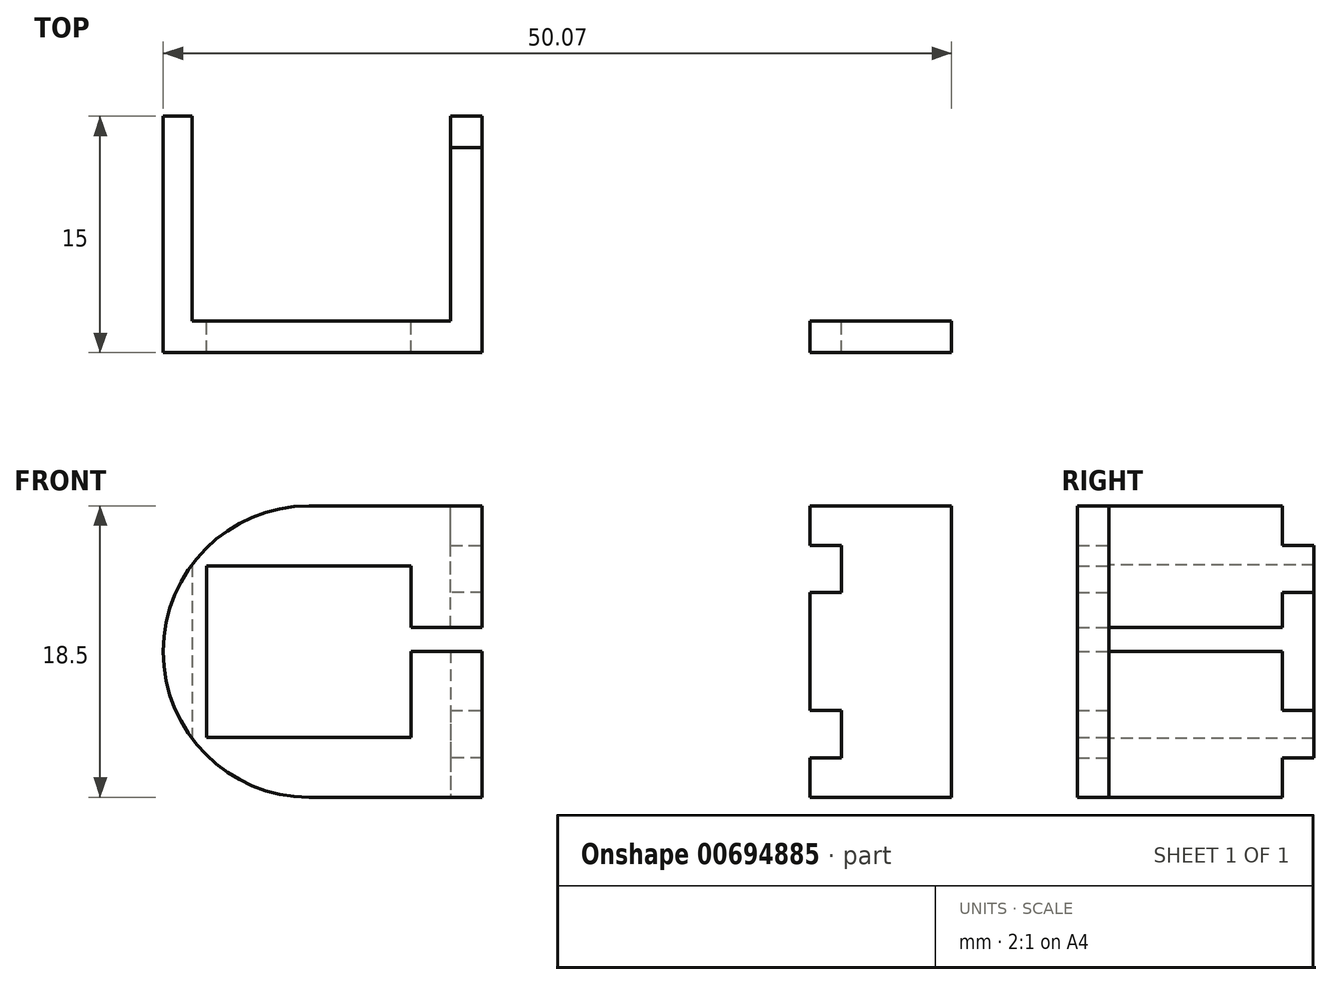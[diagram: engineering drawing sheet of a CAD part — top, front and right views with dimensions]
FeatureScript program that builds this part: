
annotation { "Feature Type Name" : "Feature", "Feature Type Description" : "" }
export const myFeature = defineFeature(function(context is Context, id is Id, definition is map)
    precondition{}
    {
        {
            var Q0;
            Q0=qCreatedBy(makeId("Front.planeOp"),FACE);
            var sketch = newSketch(context, id + "F0", { "sketchPlane" : qUnion([Q0])});
            skArc(sketch, "E0.MirrorCS", {"start": v(27.93, 0) * mm, "mid": v(18.68, 9.25) * mm, "end": v(27.93, 18.5) * mm});
            skLineSegment(sketch, "E1.MirrorCS", {"start": v(20.5, 14.75) * mm, "end": v(20.5, 3.75) * mm});
            skLineSegment(sketch, "E2.MirrorCS", {"start": v(21.43, 14.7) * mm, "end": v(21.43, 3.8) * mm});
            skLineSegment(sketch, "E3.MirrorCS", {"start": v(34.43, 14.7) * mm, "end": v(21.43, 14.7) * mm});
            skLineSegment(sketch, "E4.MirrorCS", {"start": v(34.43, 3.8) * mm, "end": v(21.43, 3.8) * mm});
            skLineSegment(sketch, "E5.MirrorCS", {"start": v(34.43, 9.27) * mm, "end": v(34.43, 3.8) * mm});
            skLineSegment(sketch, "E6.MirrorCS", {"start": v(34.43, 10.77) * mm, "end": v(34.43, 14.7) * mm});
            skLineSegment(sketch, "E7.MirrorCS", {"start": v(34.43, 10.77) * mm, "end": v(38.93, 10.77) * mm});
            skLineSegment(sketch, "E8.MirrorCS", {"start": v(38.93, 9.27) * mm, "end": v(34.43, 9.27) * mm});
            skLineSegment(sketch, "E9.MirrorCS", {"start": v(36.93, 9.27) * mm, "end": v(36.93, 0) * mm});
            skLineSegment(sketch, "E10.MirrorCS", {"start": v(38.93, 18.5) * mm, "end": v(38.93, 0) * mm});
            skLineSegment(sketch, "E11.MirrorCS", {"start": v(38.93, 13) * mm, "end": v(36.93, 13) * mm});
            skLineSegment(sketch, "E12.MirrorCS", {"start": v(36.93, 16) * mm, "end": v(38.93, 16) * mm});
            skLineSegment(sketch, "E13.MirrorCS", {"start": v(38.93, 18.5) * mm, "end": v(36.93, 18.5) * mm});
            skLineSegment(sketch, "E14.MirrorCS", {"start": v(27.93, 18.5) * mm, "end": v(38.93, 18.5) * mm});
            skLineSegment(sketch, "E15.MirrorCS", {"start": v(27.93, 0) * mm, "end": v(38.93, 0) * mm});
            skLineSegment(sketch, "E16.MirrorCS", {"start": v(36.93, 10.77) * mm, "end": v(36.93, 18.5) * mm});
            skLineSegment(sketch, "E17.MirrorCS", {"start": v(36.93, 5.5) * mm, "end": v(38.93, 5.5) * mm});
            skLineSegment(sketch, "E18.MirrorCS", {"start": v(38.93, 2.5) * mm, "end": v(36.93, 2.5) * mm});
            skLineSegment(sketch, "E19.MirrorCS", {"start": v(59.75, 18.5) * mm, "end": v(61.75, 18.5) * mm});
            skLineSegment(sketch, "E20.MirrorCS", {"start": v(59.75, 18.5) * mm, "end": v(59.75, 16) * mm});
            skLineSegment(sketch, "E21.MirrorCS", {"start": v(61.75, 16) * mm, "end": v(59.75, 16) * mm});
            skLineSegment(sketch, "E22.MirrorCS", {"start": v(59.75, 16) * mm, "end": v(59.75, 18.5) * mm});
            skLineSegment(sketch, "E23.MirrorCS", {"start": v(61.75, 13) * mm, "end": v(61.75, 16) * mm});
            skLineSegment(sketch, "E24.MirrorCS", {"start": v(59.75, 13) * mm, "end": v(61.75, 13) * mm});
            skLineSegment(sketch, "E25.MirrorCS", {"start": v(59.75, 16) * mm, "end": v(59.75, 13.5) * mm});
            skLineSegment(sketch, "E26.MirrorCS", {"start": v(61.75, 5.5) * mm, "end": v(59.75, 5.5) * mm});
            skLineSegment(sketch, "E27.MirrorCS", {"start": v(61.75, 2.5) * mm, "end": v(59.75, 2.5) * mm});
            skLineSegment(sketch, "E28.MirrorCS", {"start": v(59.75, 0) * mm, "end": v(59.75, 18.5) * mm});
            skLineSegment(sketch, "E29.MirrorCS", {"start": v(68.75, 0) * mm, "end": v(68.75, 18.5) * mm});
            skLineSegment(sketch, "E30.MirrorCS", {"start": v(59.75, 0) * mm, "end": v(68.75, 0) * mm});
            skLineSegment(sketch, "E31.MirrorCS", {"start": v(61.75, 0) * mm, "end": v(61.75, 18.5) * mm});
            skLineSegment(sketch, "E32.MirrorCS", {"start": v(59.75, 18.5) * mm, "end": v(68.75, 18.5) * mm});
            skLineSegment(sketch, "E33.MirrorCS", {"start": v(38.93, 10.77) * mm, "end": v(38.93, 9.27) * mm});
            skLineSegment(sketch, "E34.MirrorCS", {"start": v(36.93, 18.5) * mm, "end": v(36.93, 16) * mm});
            skLineSegment(sketch, "E35.MirrorCS", {"start": v(36.93, 13) * mm, "end": v(36.93, 16) * mm});
            skPoint(sketch, "E36.MirrorP", {"position": v(37.93, 13) * mm});
            skLineSegment(sketch, "E37.MirrorCS", {"start": v(27.93, 0) * mm, "end": v(27.93, 18.5) * mm});
            skSolve(sketch);
        }
        {
            var Q0;
            {var subQ3=sQuery(id+"F0.wireOp",EDGE,"kESMrQ5b-ams2-7Oer-iUNR-JSe8RSim2Rgg");Q0=makeQuery(id+"F0.imprint","IMPRINT",FACE,{"disambiguationData":[TD([[makeQuery(id+"F0.imprint","IMPRINT",EDGE,{"derivedFrom":subQ3}),-1.0]])]});}
            var Q1;
            {var subQ12=sQuery(id+"F0.wireOp",EDGE,"Yr70NcdM-JPDj-xeuz-Pe8b-xZYOvRdpObg3.top");Q1=makeQuery(id+"F0.imprint","IMPRINT",FACE,{"disambiguationData":[TD([[makeQuery(id+"F0.imprint","IMPRINT",EDGE,{"derivedFrom":subQ12}),1.0]])]});}
            var Q2;
            {var subQ0=sQuery(id+"F0.wireOp",EDGE,"UIRKKA4R-8CtD-udC1-kdKj-49Blse4cZEUQ");Q2=makeQuery(id+"F0.imprint","IMPRINT",FACE,{"disambiguationData":[TD([[makeQuery(id+"F0.imprint","IMPRINT",EDGE,{"derivedFrom":subQ0}),-1.0]])]});}
            var Q3;
            {var subQ0=sQuery(id+"F0.wireOp",EDGE,"kkTMgRkU-buEo-ValQ-K1kS-Wfla19uNzp3g");Q3=makeQuery(id+"F0.imprint","IMPRINT",FACE,{"disambiguationData":[TD([[makeQuery(id+"F0.imprint","IMPRINT",EDGE,{"derivedFrom":subQ0}),-1.0]])]});}
            var Q4;
            {var subQ5=sQuery(id+"F0.wireOp",EDGE,"umQxmC7r-UdGl-FK5S-hts2-lfyIpxZBKDAi");Q4=makeQuery(id+"F0.imprint","IMPRINT",FACE,{"disambiguationData":[TD([[makeQuery(id+"F0.imprint","IMPRINT",EDGE,{"derivedFrom":subQ5}),-1.0]])]});}
            var Q5;
            {var subQ0=sQuery(id+"F0.wireOp",EDGE,"kNnYodP8-lzwz-CTh5-yjqH-wt2QJZLzKjdq");Q5=makeQuery(id+"F0.imprint","IMPRINT",FACE,{"disambiguationData":[TD([[makeQuery(id+"F0.imprint","IMPRINT",EDGE,{"derivedFrom":subQ0}),1.0]])]});}
            var Q6;
            {var subQ0=sQuery(id+"F0.wireOp",EDGE,"b358ca5a-2aeb-42fa-86b1-f23f205046210.MirrorCS");Q6=makeQuery(id+"F0.imprint","IMPRINT",FACE,{"disambiguationData":[TD([[makeQuery(id+"F0.imprint","IMPRINT",EDGE,{"derivedFrom":subQ0}),1.0]])]});}
            var Q7;
            {var subQ0=sQuery(id+"F0.wireOp",EDGE,"kESMrQ5b-ams2-7Oer-iUNR-JSe8RSim2Rgg");Q7=makeQuery(id+"F0.imprint","IMPRINT",FACE,{"disambiguationData":[TD([[makeQuery(id+"F0.imprint","IMPRINT",EDGE,{"derivedFrom":subQ0}),1.0]])]});}
            var Q8;
            {var subQ0=sQuery(id+"F0.wireOp",EDGE,"Gw2HPYI3-RblX-RLRO-vnwY-24Af2lyYfVmX");Q8=makeQuery(id+"F0.imprint","IMPRINT",FACE,{"disambiguationData":[TD([[makeQuery(id+"F0.imprint","IMPRINT",EDGE,{"derivedFrom":subQ0}),1.0]])]});}
            var Q9;
            {var subQ5=sQuery(id+"F0.wireOp",EDGE,"HoU1y5w9-Mg6P-dM28-ahBt-uTMt5Gy9G0wr.top");Q9=makeQuery(id+"F0.imprint","IMPRINT",FACE,{"disambiguationData":[TD([[makeQuery(id+"F0.imprint","IMPRINT",EDGE,{"derivedFrom":subQ5}),1.0]])]});}
            var Q10;
            {var subQ0=sQuery(id+"F0.wireOp",EDGE,"Eh2vApwt-d02c-R8fF-7La6-7nooEkv2mVzI");Q10=makeQuery(id+"F0.imprint","IMPRINT",FACE,{"disambiguationData":[TD([[makeQuery(id+"F0.imprint","IMPRINT",EDGE,{"derivedFrom":subQ0}),-1.0]])]});}
            var Q11;
            {var subQ5=sQuery(id+"F0.wireOp",EDGE,"BYSS7cPW-qHzp-sYkC-vpLU-CWsCZryCfv40");Q11=makeQuery(id+"F0.imprint","IMPRINT",FACE,{"disambiguationData":[TD([[makeQuery(id+"F0.imprint","IMPRINT",EDGE,{"derivedFrom":subQ5}),-1.0]])]});}
            var Q12;
            {var subQ0=sQuery(id+"F0.wireOp",EDGE,"XT7nVcgO-UEf4-OPxw-r3u4-JfJbnklFrjmP");Q12=makeQuery(id+"F0.imprint","IMPRINT",FACE,{"disambiguationData":[TD([[makeQuery(id+"F0.imprint","IMPRINT",EDGE,{"derivedFrom":subQ0}),-1.0]])]});}
            var Q13;
            {var subQ0=sQuery(id+"F0.wireOp",EDGE,"b358ca5a-2aeb-42fa-86b1-f23f205046210.MirrorCS");Q13=makeQuery(id+"F0.imprint","IMPRINT",FACE,{"disambiguationData":[TD([[makeQuery(id+"F0.imprint","IMPRINT",EDGE,{"derivedFrom":subQ0}),-1.0]])]});}
            var Q14;
            {var subQ0=sQuery(id+"F0.wireOp",EDGE,"WBQ6mxBe-h86F-VuFz-AZL1-RZkuSRZ2fsff");Q14=makeQuery(id+"F0.imprint","IMPRINT",FACE,{"disambiguationData":[TD([[makeQuery(id+"F0.imprint","IMPRINT",EDGE,{"derivedFrom":subQ0}),1.0]])]});}
            var Q15;
            {var subQ3=sQuery(id+"F0.wireOp",EDGE,"E6.MirrorCS");Q15=makeQuery(id+"F0.imprint","IMPRINT",FACE,{"disambiguationData":[TD([[makeQuery(id+"F0.imprint","IMPRINT",EDGE,{"derivedFrom":subQ3}),-1.0]])]});}
            var Q16;
            {var subQ3=sQuery(id+"F0.wireOp",EDGE,"E1.MirrorCS");Q16=makeQuery(id+"F0.imprint","IMPRINT",FACE,{"disambiguationData":[TD([[makeQuery(id+"F0.imprint","IMPRINT",EDGE,{"derivedFrom":subQ3}),1.0]])]});}
            var Q17;
            {var subQ5=sQuery(id+"F0.wireOp",EDGE,"E5.MirrorCS");Q17=makeQuery(id+"F0.imprint","IMPRINT",FACE,{"disambiguationData":[TD([[makeQuery(id+"F0.imprint","IMPRINT",EDGE,{"derivedFrom":subQ5}),1.0]])]});}
            var Q18;
            {var subQ3=sQuery(id+"F0.wireOp",EDGE,"E12.MirrorCS");Q18=makeQuery(id+"F0.imprint","IMPRINT",FACE,{"disambiguationData":[TD([[makeQuery(id+"F0.imprint","IMPRINT",EDGE,{"derivedFrom":subQ3}),1.0]])]});}
            var Q19;
            {var subQ0=sQuery(id+"F0.wireOp",EDGE,"E11.MirrorCS");Q19=makeQuery(id+"F0.imprint","IMPRINT",FACE,{"disambiguationData":[TD([[makeQuery(id+"F0.imprint","IMPRINT",EDGE,{"derivedFrom":subQ0}),-1.0]])]});}
            var Q20;
            {var subQ3=sQuery(id+"F0.wireOp",EDGE,"E11.MirrorCS");Q20=makeQuery(id+"F0.imprint","IMPRINT",FACE,{"disambiguationData":[TD([[makeQuery(id+"F0.imprint","IMPRINT",EDGE,{"derivedFrom":subQ3}),1.0]])]});}
            var Q21;
            {var subQ5=sQuery(id+"F0.wireOp",EDGE,"E17.MirrorCS");Q21=makeQuery(id+"F0.imprint","IMPRINT",FACE,{"disambiguationData":[TD([[makeQuery(id+"F0.imprint","IMPRINT",EDGE,{"derivedFrom":subQ5}),1.0]])]});}
            var Q22;
            {var subQ0=sQuery(id+"F0.wireOp",EDGE,"E17.MirrorCS");Q22=makeQuery(id+"F0.imprint","IMPRINT",FACE,{"disambiguationData":[TD([[makeQuery(id+"F0.imprint","IMPRINT",EDGE,{"derivedFrom":subQ0}),-1.0]])]});}
            var Q23;
            {var subQ3=sQuery(id+"F0.wireOp",EDGE,"E18.MirrorCS");Q23=makeQuery(id+"F0.imprint","IMPRINT",FACE,{"disambiguationData":[TD([[makeQuery(id+"F0.imprint","IMPRINT",EDGE,{"derivedFrom":subQ3}),1.0]])]});}
            var Q24;
            {var subQ3=sQuery(id+"F0.wireOp",EDGE,"E29.MirrorCS");Q24=makeQuery(id+"F0.imprint","IMPRINT",FACE,{"disambiguationData":[TD([[makeQuery(id+"F0.imprint","IMPRINT",EDGE,{"derivedFrom":subQ3}),1.0]])]});}
            var Q25;
            {var subQ0=sQuery(id+"F0.wireOp",EDGE,"E21.MirrorCS");Q25=makeQuery(id+"F0.imprint","IMPRINT",FACE,{"disambiguationData":[TD([[makeQuery(id+"F0.imprint","IMPRINT",EDGE,{"derivedFrom":subQ0}),-1.0]])]});}
            var Q26;
            {var subQ0=sQuery(id+"F0.wireOp",EDGE,"E24.MirrorCS");Q26=makeQuery(id+"F0.imprint","IMPRINT",FACE,{"disambiguationData":[TD([[makeQuery(id+"F0.imprint","IMPRINT",EDGE,{"derivedFrom":subQ0}),-1.0]])]});}
            var Q27;
            {var subQ0=sQuery(id+"F0.wireOp",EDGE,"E27.MirrorCS");Q27=makeQuery(id+"F0.imprint","IMPRINT",FACE,{"disambiguationData":[TD([[makeQuery(id+"F0.imprint","IMPRINT",EDGE,{"derivedFrom":subQ0}),1.0]])]});}
            var Q28;
            {var subQ0=sQuery(id+"F0.wireOp",EDGE,"E1.MirrorCS");Q28=makeQuery(id+"F0.imprint","IMPRINT",FACE,{"disambiguationData":[TD([[makeQuery(id+"F0.imprint","IMPRINT",EDGE,{"derivedFrom":subQ0}),-1.0]])]});}
            extrude(context, id + "F1", {"entities" : qUnion([Q0, Q1, Q2, Q3, Q4, Q5, Q6, Q7, Q8, Q9, Q10, Q11, Q12, Q13, Q14, Q15, Q16, Q17, Q18, Q19, Q20, Q21, Q22, Q23, Q24, Q25, Q26, Q27, Q28]), "depth" : 2 * mm, "offsetDistance" : 25 * mm});
        }
        {
            var Q0;
            {var subQ0=sQuery(id+"F0.wireOp",EDGE,"kESMrQ5b-ams2-7Oer-iUNR-JSe8RSim2Rgg");Q0=makeQuery(id+"F0.imprint","IMPRINT",FACE,{"disambiguationData":[TD([[makeQuery(id+"F0.imprint","IMPRINT",EDGE,{"derivedFrom":subQ0}),1.0]])]});}
            var Q1;
            {var subQ0=sQuery(id+"F0.wireOp",EDGE,"kNnYodP8-lzwz-CTh5-yjqH-wt2QJZLzKjdq");Q1=makeQuery(id+"F0.imprint","IMPRINT",FACE,{"disambiguationData":[TD([[makeQuery(id+"F0.imprint","IMPRINT",EDGE,{"derivedFrom":subQ0}),1.0]])]});}
            var Q2;
            {var subQ0=sQuery(id+"F0.wireOp",EDGE,"b358ca5a-2aeb-42fa-86b1-f23f205046210.MirrorCS");Q2=makeQuery(id+"F0.imprint","IMPRINT",FACE,{"disambiguationData":[TD([[makeQuery(id+"F0.imprint","IMPRINT",EDGE,{"derivedFrom":subQ0}),1.0]])]});}
            var Q3;
            {var subQ0=sQuery(id+"F0.wireOp",EDGE,"E11.MirrorCS");Q3=makeQuery(id+"F0.imprint","IMPRINT",FACE,{"disambiguationData":[TD([[makeQuery(id+"F0.imprint","IMPRINT",EDGE,{"derivedFrom":subQ0}),-1.0]])]});}
            var Q4;
            {var subQ0=sQuery(id+"F0.wireOp",EDGE,"E17.MirrorCS");Q4=makeQuery(id+"F0.imprint","IMPRINT",FACE,{"disambiguationData":[TD([[makeQuery(id+"F0.imprint","IMPRINT",EDGE,{"derivedFrom":subQ0}),-1.0]])]});}
            var Q5;
            {var subQ0=sQuery(id+"F0.wireOp",EDGE,"E1.MirrorCS");Q5=makeQuery(id+"F0.imprint","IMPRINT",FACE,{"disambiguationData":[TD([[makeQuery(id+"F0.imprint","IMPRINT",EDGE,{"derivedFrom":subQ0}),-1.0]])]});}
            extrude(context, id + "F2", {"entities" : qUnion([Q0, Q1, Q2, Q3, Q4, Q5]), "operationType" : NewBodyOperationType.ADD, "depth" : -13 * mm, "offsetDistance" : 25 * mm});
        }
        {
            var Q0;
            {var subQ0=sQuery(id+"F0.wireOp",EDGE,"UIRKKA4R-8CtD-udC1-kdKj-49Blse4cZEUQ");Q0=makeQuery(id+"F0.imprint","IMPRINT",FACE,{"disambiguationData":[TD([[makeQuery(id+"F0.imprint","IMPRINT",EDGE,{"derivedFrom":subQ0}),-1.0]])]});}
            var Q1;
            {var subQ0=sQuery(id+"F0.wireOp",EDGE,"kkTMgRkU-buEo-ValQ-K1kS-Wfla19uNzp3g");Q1=makeQuery(id+"F0.imprint","IMPRINT",FACE,{"disambiguationData":[TD([[makeQuery(id+"F0.imprint","IMPRINT",EDGE,{"derivedFrom":subQ0}),-1.0]])]});}
            var Q2;
            {var subQ5=sQuery(id+"F0.wireOp",EDGE,"umQxmC7r-UdGl-FK5S-hts2-lfyIpxZBKDAi");Q2=makeQuery(id+"F0.imprint","IMPRINT",FACE,{"disambiguationData":[TD([[makeQuery(id+"F0.imprint","IMPRINT",EDGE,{"derivedFrom":subQ5}),-1.0]])]});}
            var Q3;
            {var subQ0=sQuery(id+"F0.wireOp",EDGE,"b358ca5a-2aeb-42fa-86b1-f23f205046210.MirrorCS");Q3=makeQuery(id+"F0.imprint","IMPRINT",FACE,{"disambiguationData":[TD([[makeQuery(id+"F0.imprint","IMPRINT",EDGE,{"derivedFrom":subQ0}),-1.0]])]});}
            var Q4;
            {var subQ3=sQuery(id+"F0.wireOp",EDGE,"E12.MirrorCS");Q4=makeQuery(id+"F0.imprint","IMPRINT",FACE,{"disambiguationData":[TD([[makeQuery(id+"F0.imprint","IMPRINT",EDGE,{"derivedFrom":subQ3}),1.0]])]});}
            var Q5;
            {var subQ3=sQuery(id+"F0.wireOp",EDGE,"E11.MirrorCS");Q5=makeQuery(id+"F0.imprint","IMPRINT",FACE,{"disambiguationData":[TD([[makeQuery(id+"F0.imprint","IMPRINT",EDGE,{"derivedFrom":subQ3}),1.0]])]});}
            var Q6;
            {var subQ5=sQuery(id+"F0.wireOp",EDGE,"E17.MirrorCS");Q6=makeQuery(id+"F0.imprint","IMPRINT",FACE,{"disambiguationData":[TD([[makeQuery(id+"F0.imprint","IMPRINT",EDGE,{"derivedFrom":subQ5}),1.0]])]});}
            var Q7;
            {var subQ3=sQuery(id+"F0.wireOp",EDGE,"E18.MirrorCS");Q7=makeQuery(id+"F0.imprint","IMPRINT",FACE,{"disambiguationData":[TD([[makeQuery(id+"F0.imprint","IMPRINT",EDGE,{"derivedFrom":subQ3}),1.0]])]});}
            extrude(context, id + "F3", {"entities" : qUnion([Q0, Q1, Q2, Q3, Q4, Q5, Q6, Q7]), "operationType" : NewBodyOperationType.ADD, "depth" : -11 * mm, "offsetDistance" : 25 * mm});
        }
    });
